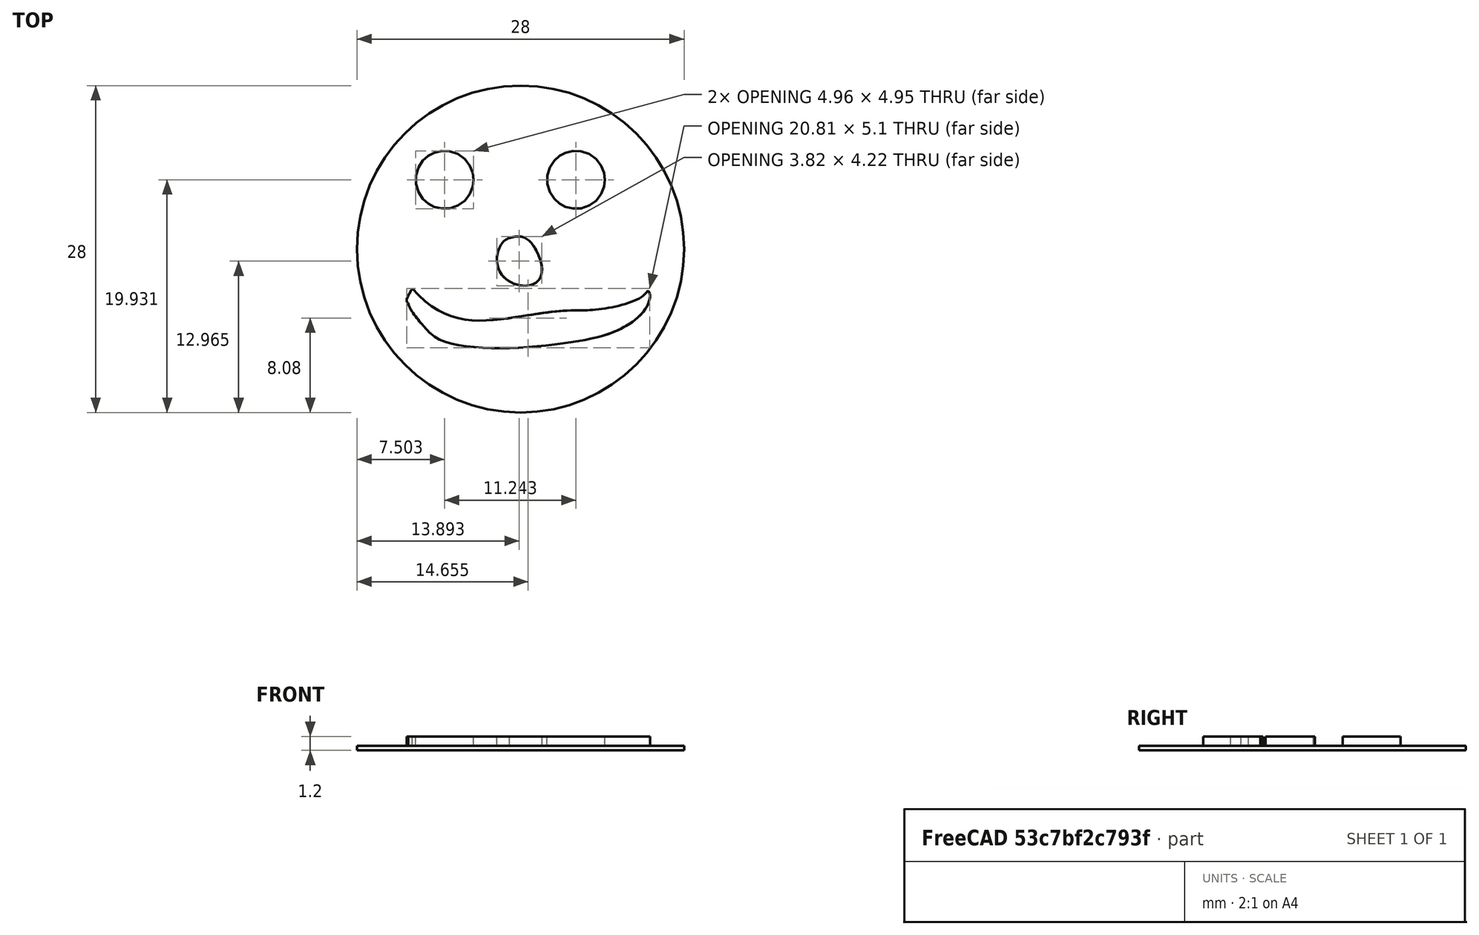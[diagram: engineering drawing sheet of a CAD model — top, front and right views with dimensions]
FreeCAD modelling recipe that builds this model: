
FCSTD DOCUMENT  (FreeCAD 0.18R14975 (Git))
Label: Medallion Face Test Rev A
License: All rights reserved
LicenseURL: http://en.wikipedia.org/wiki/All_rights_reserved
objects: Sketcher::SketchObject×2, PartDesign::Pad×2, Part::Part2DObjectPython×1, PartDesign::Body×1
note: 8 computed .brp shape members not serialized (recipe doc carries the construction recipe); baked Part::Feature solids carry a one-line shape summary decoded from their .brp

FEATURE [Sketcher::SketchObject] Sketch  label="Face Base Profile"
  MapMode = 5
  Support = -> [XY_Plane]
  sketch-geometry (1):
    g0: Circle CenterX=0 CenterY=0 CenterZ=0 NormalX=0 NormalY=0 NormalZ=1 AngleXU=0 Radius=14
  constraints (2):
    c: Coincident(g0,g-1)
    c: Radius(g0) = 14
FEATURE [PartDesign::Pad] Pad  label="Face Base"
  Length = 0.4
  Length2 = 100
  Profile = -> Sketch
  Type = 0
FEATURE [Sketcher::SketchObject] Sketch005
  Placement = pos=(-86.4048,117.218,0) rot=(0,0,1;0rad)
  sketch-geometry (11):
    g0: BSplineCurve PolesCount=7 KnotsCount=4 Degree=2 IsPeriodic=0
    g1: BSplineCurve PolesCount=4 KnotsCount=2 Degree=3 IsPeriodic=0
    g2: BSplineCurve PolesCount=4 KnotsCount=2 Degree=3 IsPeriodic=0
    g3: BSplineCurve PolesCount=4 KnotsCount=2 Degree=3 IsPeriodic=0
    g4: BSplineCurve PolesCount=7 KnotsCount=4 Degree=2 IsPeriodic=0
    g5: BSplineCurve PolesCount=4 KnotsCount=2 Degree=3 IsPeriodic=0
    g6: BSplineCurve PolesCount=4 KnotsCount=2 Degree=3 IsPeriodic=0
    g7: BSplineCurve PolesCount=4 KnotsCount=2 Degree=3 IsPeriodic=0
    g8: BSplineCurve PolesCount=4 KnotsCount=2 Degree=3 IsPeriodic=0
    g9: BSplineCurve PolesCount=4 KnotsCount=2 Degree=3 IsPeriodic=0
    g10: BSplineCurve PolesCount=4 KnotsCount=2 Degree=3 IsPeriodic=0
  constraints (9):
    c: Coincident(g1,g2)
    c: Coincident(g2,g3)
    c: Coincident(g3,g1)
    c: Coincident(g5,g6)
    c: Coincident(g6,g7)
    c: Coincident(g7,g8)
    c: Coincident(g8,g9)
    c: Coincident(g9,g10)
    c: Coincident(g10,g5)
FEATURE [Part::Part2DObjectPython] Clone2D  label="Sketch005 (2D)"  # Draft 2D object (typed FeaturePython)
  Fuse = false
  Objects = -> [Sketch005]
  Placement = pos=(-15.3624,20.0267,0) rot=(0,0,1;0rad)
  Scale = (0.18,0.18,0)
FEATURE [PartDesign::Pad] Pad001  label="Pattern Emboss"
  BaseFeature = -> Pad
  Length = 1.2
  Length2 = 100
  Profile = -> Clone2D
  Type = 0
FEATURE [PartDesign::Body] Body
  Group = -> [Sketch,Pad,Clone2D,Pad001]
  Origin = -> Origin
  Tip = -> Pad001
